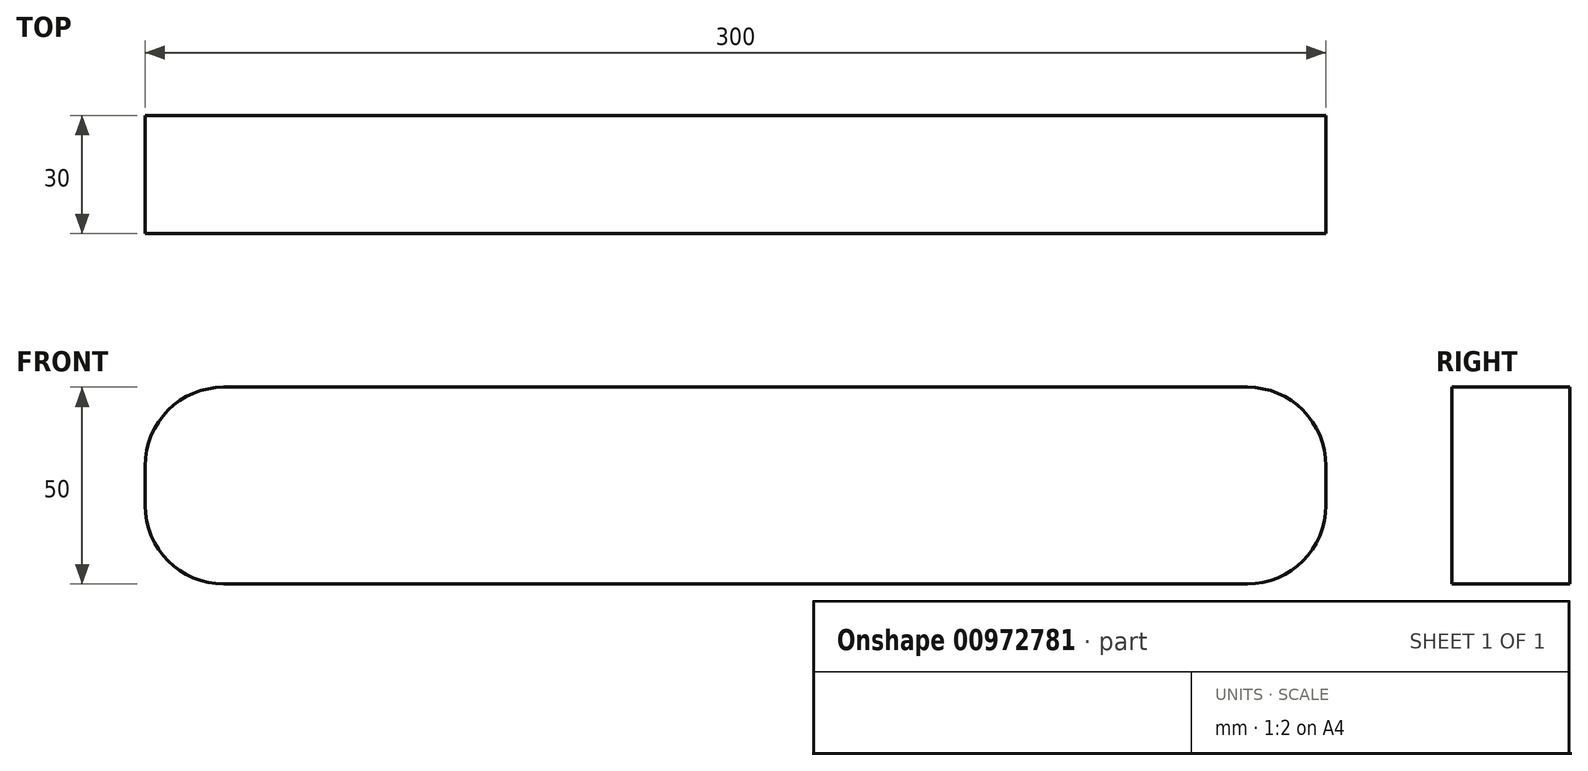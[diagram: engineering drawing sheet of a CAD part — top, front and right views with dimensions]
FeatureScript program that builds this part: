
annotation { "Feature Type Name" : "Feature", "Feature Type Description" : "" }
export const myFeature = defineFeature(function(context is Context, id is Id, definition is map)
    precondition{}
    {
        {
            var Q0;
            Q0=qCreatedBy(makeId("Front.planeOp"),FACE);
            var sketch = newSketch(context, id + "F0", { "sketchPlane" : qUnion([Q0])});
            skLineSegment(sketch, "E0.bottom", {"start": v(150, 25) * mm, "end": v(-150, 25) * mm});
            skLineSegment(sketch, "E0.top", {"start": v(150, -25) * mm, "end": v(-150, -25) * mm});
            skLineSegment(sketch, "E0.left", {"start": v(150, 25) * mm, "end": v(150, -25) * mm});
            skLineSegment(sketch, "E0.right", {"start": v(-150, 25) * mm, "end": v(-150, -25) * mm});
            skPoint(sketch, "E0.middle", {"position": v(0, 0) * mm});
            skSolve(sketch);
        }
        {
            var Q0;
            Q0 = qSketchRegion(id + "F0", true);
            extrude(context, id + "F1", {"entities" : qUnion([Q0]), "depth" : 15 * mm, "offsetDistance" : 25.4 * mm, "hasSecondDirection" : true, "secondDirectionOppositeDirection" : true, "secondDirectionDepth" : 15 * mm});
        }
        {
            var Q0;
            Q0=makeQuery(id+"F1.opExtrude","SWEPT_EDGE",EDGE,{"disambiguationData":[OSD([sQuery(id+"F0.wireOp",EDGE,"E0.bottom"),sQuery(id+"F0.wireOp",EDGE,"E0.left")])]});
            var Q1;
            Q1=makeQuery(id+"F1.opExtrude","SWEPT_EDGE",EDGE,{"disambiguationData":[OSD([sQuery(id+"F0.wireOp",EDGE,"E0.top"),sQuery(id+"F0.wireOp",EDGE,"E0.left")])]});
            var Q2;
            Q2=makeQuery(id+"F1.opExtrude","SWEPT_EDGE",EDGE,{"disambiguationData":[OSD([sQuery(id+"F0.wireOp",EDGE,"E0.bottom"),sQuery(id+"F0.wireOp",EDGE,"E0.right")])]});
            var Q3;
            Q3=makeQuery(id+"F1.opExtrude","SWEPT_EDGE",EDGE,{"disambiguationData":[OSD([sQuery(id+"F0.wireOp",EDGE,"E0.top"),sQuery(id+"F0.wireOp",EDGE,"E0.right")])]});
            fillet(context, id + "F2", {"entities" : qUnion([Q0, Q1, Q2, Q3]), "radius" : 20 * mm, "tangentPropagation" : true, "allowEdgeOverflow" : false});
        }
    });
